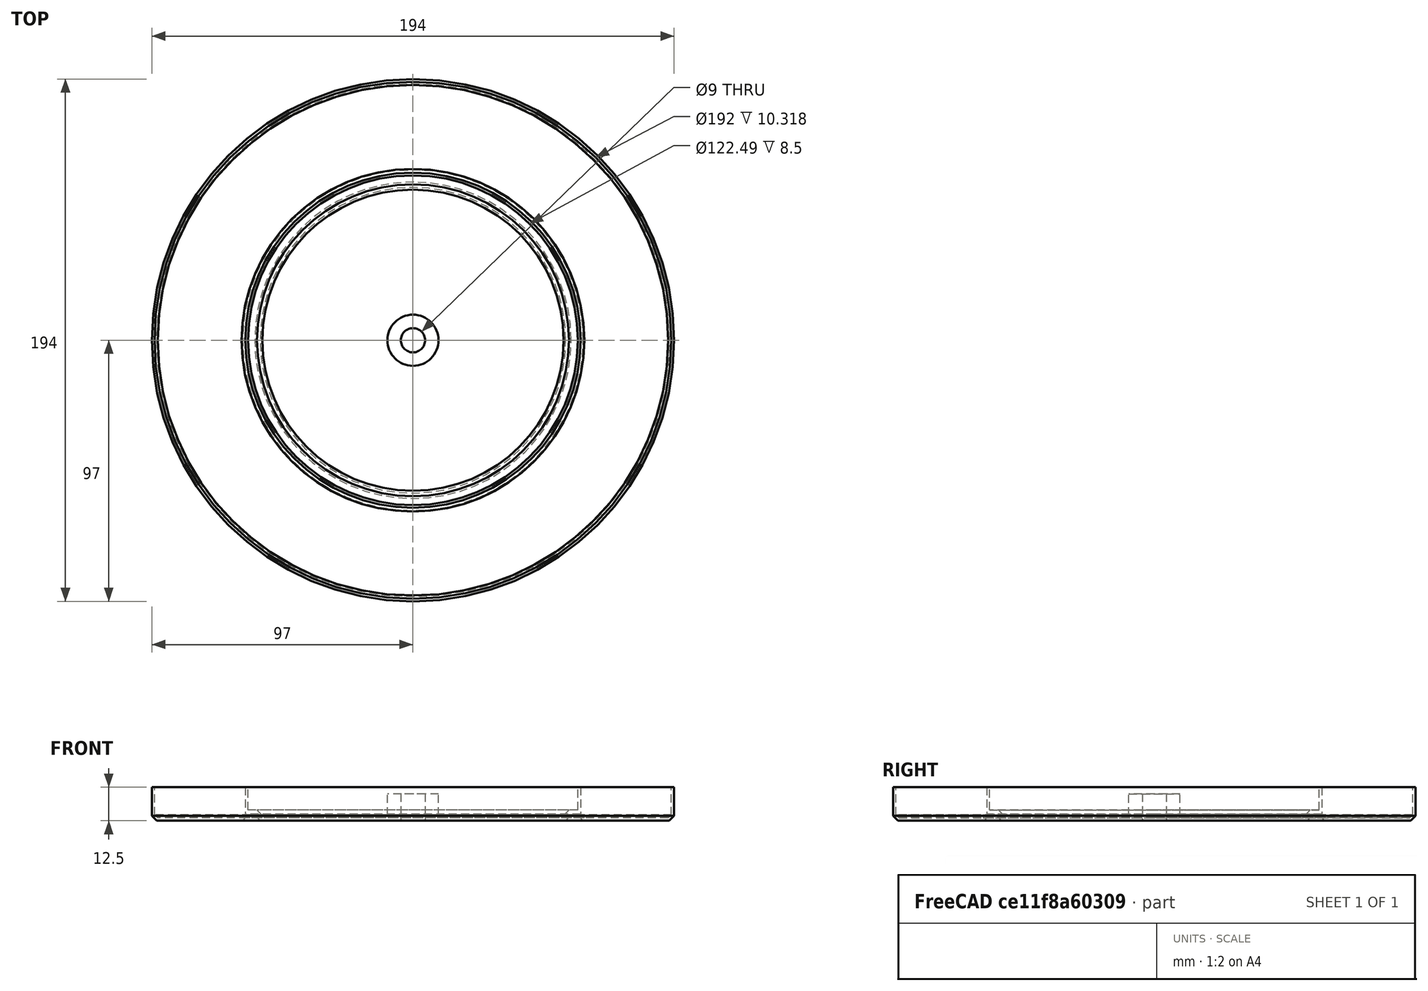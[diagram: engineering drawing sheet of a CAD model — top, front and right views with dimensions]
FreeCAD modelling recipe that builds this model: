
FCSTD DOCUMENT  (FreeCAD 0.19R24212 (Git))
Label: insert_empty
License: All rights reserved
LicenseURL: http://en.wikipedia.org/wiki/All_rights_reserved
objects: Sketcher::SketchObject×1, PartDesign::Revolution×1, PartDesign::Body×1
note: 4 computed .brp shape members not serialized (recipe doc carries the construction recipe); baked Part::Feature solids carry a one-line shape summary decoded from their .brp

FEATURE [Sketcher::SketchObject] Sketch
  FullyConstrained = true
  MapMode = 5
  Placement = pos=(0,0,0) rot=(1,0,0;1.5708rad)
  Support = -> [XZ_Plane]
  sketch-geometry (25):
    g0: LineSegment StartX=4.5 StartY=10 StartZ=0 EndX=4.5 EndY=0 EndZ=0
    g1: LineSegment StartX=4.5 StartY=0 StartZ=0 EndX=56.7574 EndY=0 EndZ=0
    g2: LineSegment StartX=56.7574 StartY=0 StartZ=0 EndX=58.7574 EndY=2 EndZ=0
    g3: LineSegment StartX=58.7574 StartY=2 StartZ=0 EndX=61.2426 EndY=2 EndZ=0
    g4: LineSegment StartX=61.2426 StartY=2 StartZ=0 EndX=63.2426 EndY=0 EndZ=0
    g5: LineSegment StartX=63.2426 StartY=0 StartZ=0 EndX=95.2322 EndY=0 EndZ=0
    g6: LineSegment StartX=97 StartY=12.5 StartZ=0 EndX=96 EndY=12.5 EndZ=0
    g7: LineSegment StartX=55.9289 StartY=2 StartZ=0 EndX=9.5 EndY=2 EndZ=0
    g8: LineSegment StartX=9.5 StartY=2 StartZ=0 EndX=9.5 EndY=10 EndZ=0
    g9: LineSegment StartX=9.5 StartY=10 StartZ=0 EndX=4.5 EndY=10 EndZ=0
    g10: Circle CenterX=60 CenterY=-1 CenterZ=0 NormalX=0 NormalY=0 NormalZ=1 AngleXU=0 Radius=3
    g11: LineSegment StartX=56.7574 StartY=0 StartZ=0 EndX=63.2426 EndY=0 EndZ=0
    g12: LineSegment StartX=97 StartY=12.5 StartZ=0 EndX=97 EndY=1.76777 EndZ=0
    g13: LineSegment StartX=95.2322 StartY=0 StartZ=0 EndX=97 EndY=1.76777 EndZ=0
    g14: LineSegment StartX=55.9289 StartY=2 StartZ=0 EndX=57.9289 EndY=4 EndZ=0
    g15: LineSegment StartX=57.9289 StartY=4 StartZ=0 EndX=61.2426 EndY=4 EndZ=0
    g16: LineSegment StartX=61.2426 StartY=4 StartZ=0 EndX=61.2426 EndY=12.5 EndZ=0
    g17: LineSegment StartX=61.2426 StartY=2 StartZ=0 EndX=61.2426 EndY=4 EndZ=0
    g18: LineSegment StartX=61.2426 StartY=12.5 StartZ=0 EndX=62.2426 EndY=12.5 EndZ=0
    g19: LineSegment StartX=62.2426 StartY=12.5 StartZ=0 EndX=62.2426 EndY=2.41421 EndZ=0
    g20: LineSegment StartX=62.2426 StartY=2.41421 StartZ=0 EndX=63.6569 EndY=1 EndZ=0
    g21: LineSegment StartX=63.6569 StartY=1 StartZ=0 EndX=94.818 EndY=1 EndZ=0
    g22: LineSegment StartX=94.818 StartY=1 StartZ=0 EndX=96 EndY=2.18198 EndZ=0
    g23: LineSegment StartX=96 StartY=2.18198 StartZ=0 EndX=96 EndY=12.5 EndZ=0
    g24: LineSegment StartX=62.2426 StartY=12.5 StartZ=0 EndX=96 EndY=12.5 EndZ=0
  constraints (72):
    c: PointOnObject(g0,g-1)
    c: Vertical(g0)
    c: Coincident(g0,g1)
    c: Horizontal(g1)
    c: Coincident(g1,g2)
    c: Coincident(g2,g3)
    c: Horizontal(g3)
    c: Coincident(g3,g4)
    c: PointOnObject(g4,g-1)
    c: Coincident(g4,g5)
    c: Horizontal(g6)
    c: Horizontal(g7)
    c: Coincident(g7,g8)
    c: Vertical(g8)
    c: Coincident(g8,g9)
    c: Coincident(g9,g0)
    c: Horizontal(g9)
    c: Radius(g10) = 3
    c: Tangent(g10,g3)
    c: Tangent(g10,g4)
    c: Tangent(g10,g2)
    c: Coincident(g11,g1)
    c: Coincident(g11,g4)
    c: Angle(g11,g2) = 0.785398
    c: Angle(g4,g11) = 0.785398
    c: Distance(g10,g11) = 1
    c: DistanceX(g-1,g10) = 60
    c: DistanceX(g-1,g0) = 4.5
    c: Distance(g0) = 10
    c: Distance(g9) = 5
    c: Distance(g7,g1) = 2
    c: Horizontal(g5)
    c: Coincident(g12,g6)
    c: Vertical(g12)
    c: Coincident(g13,g5)
    c: Coincident(g13,g12)
    c: DistanceX(g-1,g12) = 97
    c: Distance(g13) = 2.5
    c: Angle(g13,g5) = 2.35619
    c: DistanceY(g-1,g6) = 12.5
    c: Coincident(g7,g14)
    c: Coincident(g14,g15)
    c: Horizontal(g15)
    c: Coincident(g15,g16)
    c: Vertical(g16)
    c: Coincident(g17,g3)
    c: Coincident(g17,g15)
    c: Vertical(g17)
    c: Angle(g14,g7) = 2.35619
    c: Distance(g17) = 2
    c: Distance(g1,g14) = 2
    c: Coincident(g16,g18)
    c: Coincident(g18,g19)
    c: Vertical(g19)
    c: Coincident(g19,g20)
    c: Coincident(g20,g21)
    c: Horizontal(g21)
    c: Coincident(g21,g22)
    c: Coincident(g22,g23)
    c: Coincident(g23,g6)
    c: Vertical(g23)
    c: Parallel(g22,g13)
    c: Distance(g21,g5) = 1
    c: Distance(g6) = 1
    c: Distance(g22,g13) = 1
    c: Horizontal(g18)
    c: Coincident(g24,g18)
    c: Coincident(g24,g6)
    c: Horizontal(g24)
    c: Distance(g18) = 1
    c: Distance(g19,g4) = 1
    c: Parallel(g20,g4)
FEATURE [PartDesign::Revolution] Revolution
  Angle = 360
  Axis = (0,2e-16,1)
  Base = (0,0,0)
  Placement = pos=(0,0,0) rot=(1,0,0;1.5708rad)
  Profile = -> Sketch
  ReferenceAxis = -> Sketch [V_Axis]
  Reversed = true
FEATURE [PartDesign::Body] Body
  Group = -> [Sketch,Revolution]
  Origin = -> Origin
  Tip = -> Revolution
